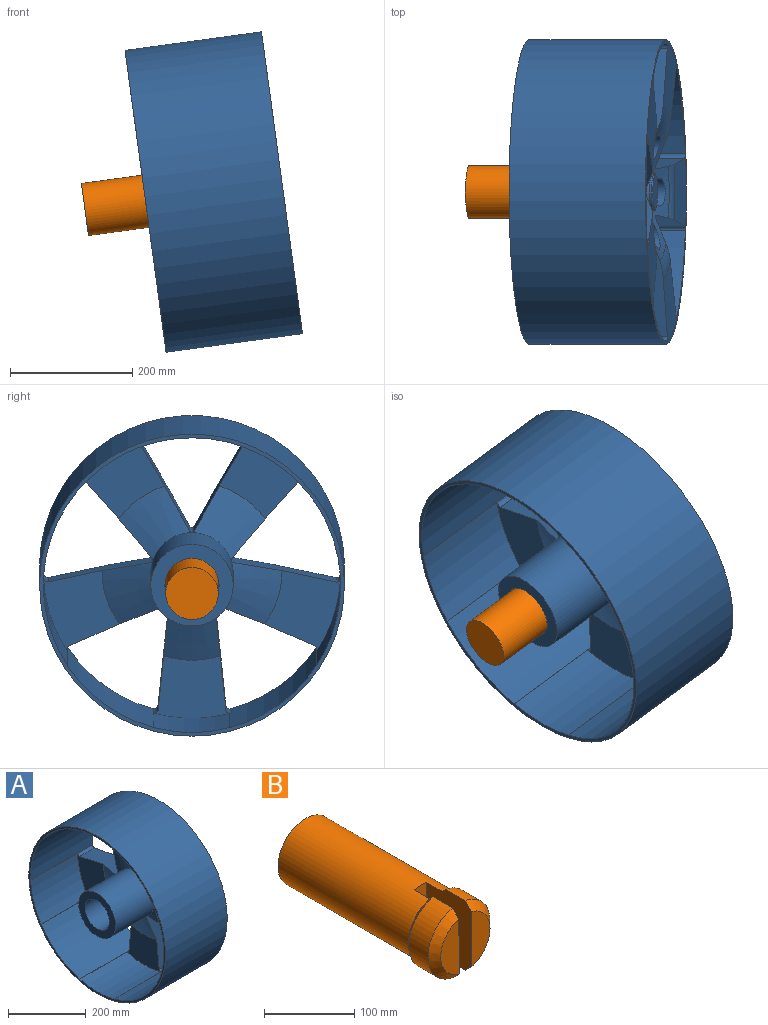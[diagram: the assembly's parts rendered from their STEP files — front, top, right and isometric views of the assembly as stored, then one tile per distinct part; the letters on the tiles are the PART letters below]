
ASSEMBLY  parts=2 mates=1
PART A: 145 faces, bbox 226x499.5x499.5 mm
  f0: cone r=67.37mm half-angle=69.4deg, axis (1,0,0), area 7405mm2, adj f36,f40,f42,f45,f134,f139
  f1: cone r=67.37mm half-angle=69.4deg, axis (1,0,0), area 7405mm2, adj f42,f46,f48,f51,f134,f135
  f2: cone r=67.37mm half-angle=69.4deg, axis (1,0,0), area 7405mm2, adj f24,f27,f48,f52,f134,f141
  f3: cone r=67.37mm half-angle=69.4deg, axis (1,0,0), area 7405mm2, adj f24,f28,f30,f33,f134,f143
  f4: plane 134.73x134.73mm, normal (-1,0,0), area 8092.4mm2, adj f129,f134
  f5: cone r=124.45mm half-angle=70.8deg, axis (1,0,0), area 14731.5mm2, adj f10,f11,f12,f13,f14,f20,f24,f27
  f6: cone r=243.25mm half-angle=87.6deg, axis (1,0,0), area 10747.7mm2, adj f10,f22,f44,f46,f49,f51
  f7: cone r=243.25mm half-angle=87.6deg, axis (1,0,0), area 10747.7mm2, adj f11,f22,f38,f40,f43,f45
  f8: cone r=243.25mm half-angle=87.6deg, axis (1,0,0), area 10747.7mm2, adj f12,f22,f32,f34,f37,f39
  f9: cone r=243.25mm half-angle=87.6deg, axis (1,0,0), area 10747.7mm2, adj f13,f22,f26,f28,f31,f33
  f10: torus R=143.39mm, axis (-1,0,0), area 2642.4mm2, adj f5,f6,f46,f51
  f11: torus R=143.39mm, axis (-1,0,0), area 2642.4mm2, adj f5,f7,f40,f45
  f12: torus R=143.39mm, axis (-1,0,0), area 2642.4mm2, adj f5,f8,f34,f39
  f13: torus R=143.39mm, axis (-1,0,0), area 2642.4mm2, adj f5,f9,f28,f33
  f14: torus R=143.39mm, axis (-1,0,0), area 2642.4mm2, adj f5,f21,f27,f52
  f15: plane 498.71x498.71mm, normal (-1,0,0), area 9451.9mm2, adj f23,f25,f26,f29,f31,f32,f35,f37
  f16: plane 56.3x56.3mm, normal (1,0,0), area 2489.8mm2, adj f17
  f17: torus R=28.15mm, axis (1,0,0), area 580.8mm2, adj f16,f18
  f18: cylinder r=30.15mm len=60.3mm, axis (1,0,0), area 609.9mm2, adj f17,f19
  f19: torus R=35.15mm, axis (1,0,0), area 1577.6mm2, adj f18,f20
  f20: plane 116.68x114.86mm, normal (1,0,0), area 6129.8mm2, adj f5,f19,f54,f56,f58,f60,f62
  f21: cone r=243.25mm half-angle=87.6deg, axis (1,0,0), area 10747.7mm2, adj f14,f22,f25,f27,f50,f52
  f22: plane 498.71x498.71mm, normal (1,0,0), area 9437.7mm2, adj f6,f7,f8,f9,f21,f23,f29,f35
  f23: cylinder r=249.35mm len=498.71mm, axis (1,0,0), area 352851.2mm2, adj f15,f22
  f24: cylinder r=4.19mm len=60.02mm, axis (1,0,0), area 475mm2, adj f2,f3,f5,f27,f28
  f25: cylinder r=5.94mm len=225.22mm, axis (1,0,0), area 527.7mm2, adj f15,f21,f27,f29,f140,f141
  f26: cylinder r=7.54mm len=225.22mm, axis (1,0,0), area 632.1mm2, adj f9,f15,f28,f29,f142,f143
  f27: plane 150.67x87.83mm, normal (0,0.86,0.5), area 9440.6mm2, adj f2,f5,f14,f21,f24,f25,f141
  f28: plane 149.15x86.95mm, normal (0,-0.86,0.5), area 9346.9mm2, adj f3,f5,f9,f13,f24,f26,f143
  f29: cylinder r=243.25mm len=225.22mm, axis (1,0,0), area 40182.8mm2, adj f15,f22,f25,f26
  f30: cylinder r=4.19mm len=60.02mm, axis (1,0,0), area 475mm2, adj f3,f5,f33,f34,f144
  f31: cylinder r=5.94mm len=225.22mm, axis (1,0,0), area 527.7mm2, adj f9,f15,f33,f35,f142,f143
  f32: cylinder r=7.54mm len=225.22mm, axis (1,0,0), area 632.1mm2, adj f8,f15,f34,f35,f136,f137
  f33: plane 129.88x116.43mm, normal (0,0.74,-0.67), area 9440.6mm2, adj f3,f5,f9,f13,f30,f31,f143
  f34: plane 168.52x83.99mm, normal (0,0.21,0.98), area 9346.9mm2, adj f5,f8,f12,f30,f32,f137,f144
  f35: cylinder r=243.25mm len=225.22mm, axis (1,0,0), area 40182.8mm2, adj f15,f22,f31,f32
  f36: cylinder r=4.19mm len=60.02mm, axis (1,0,0), area 475mm2, adj f0,f5,f39,f40,f144
  f37: cylinder r=5.94mm len=225.22mm, axis (1,0,0), area 527.7mm2, adj f8,f15,f39,f41,f136,f137
  f38: cylinder r=7.54mm len=225.22mm, axis (1,0,0), area 632.1mm2, adj f7,f15,f40,f41,f138,f139
  f39: plane 159.3x84.01mm, normal (0,-0.4,-0.91), area 9440.6mm2, adj f5,f8,f12,f36,f37,f137,f144
  f40: plane 171.46x83.99mm, normal (0,0.99,0.1), area 9346.9mm2, adj f0,f5,f7,f11,f36,f38,f139
  f41: cylinder r=243.25mm len=225.22mm, axis (1,0,0), area 40182.8mm2, adj f15,f22,f37,f38
  f42: cylinder r=4.19mm len=60.02mm, axis (1,0,0), area 475mm2, adj f0,f1,f5,f45,f46
  f43: cylinder r=5.94mm len=225.22mm, axis (1,0,0), area 527.7mm2, adj f7,f15,f45,f47,f138,f139
  f44: cylinder r=7.54mm len=225.22mm, axis (1,0,0), area 632.1mm2, adj f6,f15,f46,f47,f133,f135
  f45: plane 173.21x84.02mm, normal (0,-0.99,0.1), area 9440.6mm2, adj f0,f5,f7,f11,f42,f43,f139
  f46: plane 157.7x83.99mm, normal (0,0.4,-0.91), area 9346.9mm2, adj f1,f5,f6,f10,f42,f44,f135
  f47: cylinder r=243.25mm len=225.22mm, axis (1,0,0), area 40182.8mm2, adj f15,f22,f43,f44
  f48: cylinder r=4.19mm len=60.02mm, axis (1,0,0), area 475mm2, adj f1,f2,f5,f51,f52
  f49: cylinder r=5.94mm len=225.22mm, axis (1,0,0), area 527.7mm2, adj f6,f15,f51,f53,f133,f135
  f50: cylinder r=7.54mm len=225.22mm, axis (1,0,0), area 632.1mm2, adj f15,f21,f52,f53,f140,f141
  f51: plane 170.23x84.02mm, normal (0,-0.21,0.98), area 9440.6mm2, adj f1,f5,f6,f10,f48,f49,f135
  f52: plane 128.58x115.26mm, normal (0,-0.74,-0.67), area 9346.9mm2, adj f2,f5,f14,f21,f48,f50,f141
  f53: cylinder r=243.25mm len=225.22mm, axis (1,0,0), area 40182.8mm2, adj f15,f22,f49,f50
  f54: cylinder r=23mm len=46mm, axis (1,0,0), area 4559.1mm2, adj f5,f20,f55
  f55: plane 46x46mm, normal (1,0,0), area 806.5mm2, adj f54,f64,f65,f66,f67,f68,f69
  f56: cylinder r=23mm len=46mm, axis (1,0,0), area 4559.5mm2, adj f5,f20,f57
  f57: plane 46x46mm, normal (1,0,0), area 806.5mm2, adj f56,f71,f72,f73,f74,f75,f76
  f58: cylinder r=23mm len=46mm, axis (1,0,0), area 4559.8mm2, adj f5,f20,f59
  f59: plane 46x46mm, normal (1,0,0), area 806.5mm2, adj f58,f78,f79,f80,f81,f82,f83
  f60: cylinder r=23mm len=46mm, axis (1,0,0), area 4559.8mm2, adj f5,f20,f61
  f61: plane 46x46mm, normal (1,0,0), area 806.5mm2, adj f60,f85,f86,f87,f88,f89,f90
  f62: cylinder r=23mm len=46mm, axis (1,0,0), area 4561.5mm2, adj f5,f20,f63
  f63: plane 46x46mm, normal (1,0,0), area 806.5mm2, adj f62,f92,f93,f94,f95,f96,f97
  f64: plane 19x18.14mm, normal (0,-0.01,1), area 344.8mm2, adj f55,f65,f69,f124
  f65: plane 19x15.83mm, normal (0,-0.87,0.49), area 344.8mm2, adj f55,f64,f66,f123
  f66: plane 19x15.6mm, normal (0,-0.86,-0.51), area 344.8mm2, adj f55,f65,f67,f125
  f67: plane 19x18.14mm, normal (0,0.01,-1), area 344.8mm2, adj f55,f66,f68,f127
  f68: plane 19x15.83mm, normal (0,0.87,-0.49), area 344.8mm2, adj f55,f67,f69,f128
  f69: plane 19x15.6mm, normal (0,0.86,0.51), area 344.8mm2, adj f55,f64,f68,f126
  f70: plane 31.67x27.63mm, normal (1,0,0), area 651.6mm2, adj f123,f124,f125,f126,f127,f128
  f71: plane 19x17.33mm, normal (0,-0.95,0.3), area 344.8mm2, adj f57,f72,f76,f118
  f72: plane 19x13.33mm, normal (0,-0.73,-0.68), area 344.8mm2, adj f57,f71,f73,f117
  f73: plane 19x17.7mm, normal (0,0.22,-0.98), area 344.8mm2, adj f57,f72,f74,f119
  f74: plane 19x17.33mm, normal (0,0.95,-0.3), area 344.8mm2, adj f57,f73,f75,f121
  f75: plane 19x13.33mm, normal (0,0.73,0.68), area 344.8mm2, adj f57,f74,f76,f122
  f76: plane 19x17.7mm, normal (0,-0.22,0.98), area 344.8mm2, adj f57,f71,f75,f120
  f77: plane 30.89x30.24mm, normal (1,0,0), area 651.6mm2, adj f117,f118,f119,f120,f121,f122
  f78: plane 19x14.82mm, normal (0,-0.58,-0.82), area 344.8mm2, adj f59,f79,f83,f112
  f79: plane 19x16.48mm, normal (0,0.42,-0.91), area 344.8mm2, adj f59,f78,f80,f111
  f80: plane 19x18.07mm, normal (0,1,-0.09), area 344.8mm2, adj f59,f79,f81,f113
  f81: plane 19x14.82mm, normal (0,0.58,0.82), area 344.8mm2, adj f59,f80,f82,f115
  f82: plane 19x16.48mm, normal (0,-0.42,0.91), area 344.8mm2, adj f59,f81,f83,f116
  f83: plane 19x18.07mm, normal (0,-1,0.09), area 344.8mm2, adj f59,f78,f82,f114
  f84: plane 31.54x28.77mm, normal (1,0,0), area 651.6mm2, adj f111,f112,f113,f114,f115,f116
  f85: plane 19x14.54mm, normal (0,0.6,-0.8), area 344.8mm2, adj f61,f86,f90,f106
  f86: plane 19x18.02mm, normal (0,0.99,0.12), area 344.8mm2, adj f61,f85,f87,f105
  f87: plane 19x16.67mm, normal (0,0.4,0.92), area 344.8mm2, adj f61,f86,f88,f107
  f88: plane 19x14.54mm, normal (0,-0.6,0.8), area 344.8mm2, adj f61,f87,f89,f109
  f89: plane 19x18.02mm, normal (0,-0.99,-0.12), area 344.8mm2, adj f61,f88,f90,f110
  f90: plane 19x16.67mm, normal (0,-0.4,-0.92), area 344.8mm2, adj f61,f85,f89,f108
  f91: plane 31.45x29.1mm, normal (1,0,0), area 651.6mm2, adj f105,f106,f107,f108,f109,f110
  f92: plane 19x17.18mm, normal (0,0.95,0.32), area 344.8mm2, adj f63,f93,f97,f100
  f93: plane 19x17.8mm, normal (0,0.2,0.98), area 344.8mm2, adj f63,f92,f94,f99
  f94: plane 19x13.64mm, normal (0,-0.75,0.66), area 344.8mm2, adj f63,f93,f95,f101
  f95: plane 19x17.18mm, normal (0,-0.95,-0.32), area 344.8mm2, adj f63,f94,f96,f103
  f96: plane 19x17.8mm, normal (0,-0.2,-0.98), area 344.8mm2, adj f63,f95,f97,f104
  f97: plane 19x13.64mm, normal (0,0.75,-0.66), area 344.8mm2, adj f63,f92,f96,f102
  f98: plane 31.06x30mm, normal (1,0,0), area 651.6mm2, adj f99,f100,f101,f102,f103,f104
  f99: cylinder r=2mm len=18.19mm, axis (0,0.98,-0.2), area 53.4mm2, adj f93,f98,f100,f101
  f100: cylinder r=2mm len=17.83mm, axis (0,0.32,-0.95), area 53.4mm2, adj f92,f98,f99,f102
  f101: cylinder r=2mm len=14.96mm, axis (0,0.66,0.75), area 53.4mm2, adj f94,f98,f99,f103
  f102: cylinder r=2mm len=14.96mm, axis (0,-0.66,-0.75), area 53.4mm2, adj f97,f98,f100,f104
  f103: cylinder r=2mm len=17.83mm, axis (0,-0.32,0.95), area 53.4mm2, adj f95,f98,f101,f104
  f104: cylinder r=2mm len=18.19mm, axis (0,-0.98,0.2), area 53.4mm2, adj f96,f98,f102,f103
  f105: cylinder r=2mm len=18.26mm, axis (0,0.12,-0.99), area 53.4mm2, adj f86,f91,f106,f107
  f106: cylinder r=2mm len=15.74mm, axis (0,-0.8,-0.6), area 53.4mm2, adj f85,f91,f105,f108
  f107: cylinder r=2mm len=17.46mm, axis (0,0.92,-0.4), area 53.4mm2, adj f87,f91,f105,f109
  f108: cylinder r=2mm len=17.46mm, axis (0,-0.92,0.4), area 53.4mm2, adj f90,f91,f106,f110
  f109: cylinder r=2mm len=15.74mm, axis (0,0.8,0.6), area 53.4mm2, adj f88,f91,f107,f110
  f110: cylinder r=2mm len=18.26mm, axis (0,-0.12,0.99), area 53.4mm2, adj f89,f91,f108,f109
  f111: cylinder r=2mm len=17.32mm, axis (0,-0.91,-0.42), area 53.4mm2, adj f79,f84,f112,f113
  f112: cylinder r=2mm len=15.97mm, axis (0,-0.82,0.58), area 53.4mm2, adj f78,f84,f111,f114
  f113: cylinder r=2mm len=18.25mm, axis (0,-0.09,-1), area 53.4mm2, adj f80,f84,f111,f115
  f114: cylinder r=2mm len=18.25mm, axis (0,0.09,1), area 53.4mm2, adj f83,f84,f112,f116
  f115: cylinder r=2mm len=15.97mm, axis (0,0.82,-0.58), area 53.4mm2, adj f81,f84,f113,f116
  f116: cylinder r=2mm len=17.32mm, axis (0,0.91,0.42), area 53.4mm2, adj f82,f84,f114,f115
  f117: cylinder r=2mm len=14.69mm, axis (0,-0.68,0.73), area 53.4mm2, adj f72,f77,f118,f119
  f118: cylinder r=2mm len=17.92mm, axis (0,0.3,0.95), area 53.4mm2, adj f71,f77,f117,f120
  f119: cylinder r=2mm len=18.14mm, axis (0,-0.98,-0.22), area 53.4mm2, adj f73,f77,f117,f121
  f120: cylinder r=2mm len=18.14mm, axis (0,0.98,0.22), area 53.4mm2, adj f76,f77,f118,f122
  f121: cylinder r=2mm len=17.92mm, axis (0,-0.3,-0.95), area 53.4mm2, adj f74,f77,f119,f122
  f122: cylinder r=2mm len=14.69mm, axis (0,0.68,-0.73), area 53.4mm2, adj f75,f77,f120,f121
  f123: cylinder r=2mm len=16.81mm, axis (0,0.49,0.87), area 53.4mm2, adj f65,f70,f124,f125
  f124: cylinder r=2mm len=18.17mm, axis (0,1,0.01), area 53.4mm2, adj f64,f70,f123,f126
  f125: cylinder r=2mm len=16.62mm, axis (0,-0.51,0.86), area 53.4mm2, adj f66,f70,f123,f127
  f126: cylinder r=2mm len=16.62mm, axis (0,0.51,-0.86), area 53.4mm2, adj f69,f70,f124,f128
  f127: cylinder r=2mm len=18.17mm, axis (0,-1,-0.01), area 53.4mm2, adj f67,f70,f125,f128
  f128: cylinder r=2mm len=16.81mm, axis (0,-0.49,-0.87), area 53.4mm2, adj f68,f70,f126,f127
  f129: cylinder r=44.3mm len=100mm, axis (-1,0,0), area 27832.2mm2, adj f4,f130
  f130: plane 110.47x110.47mm, normal (1,0,0), area 3420.3mm2, adj f129,f131
  f131: cylinder r=55.23mm len=110.47mm, axis (-1,0,0), area 17352.6mm2, adj f130,f132
  f132: plane 110.47x110.47mm, normal (-1,0,0), area 9584.7mm2, adj f131
  f133: cylinder r=243.23mm len=171mm, axis (-1,0,0), area 21705.5mm2, adj f15,f44,f49,f135
  f134: cylinder r=67.37mm len=141mm, axis (-1,0,0), area 59680.7mm2, adj f0,f1,f2,f3,f4,f144
  f135: plane 133.6x124.09mm, normal (-1,0,0), area 9971.5mm2, adj f1,f44,f46,f49,f51,f133
  f136: cylinder r=243.23mm len=171mm, axis (-1,0,0), area 21705.5mm2, adj f15,f32,f37,f137
  f137: plane 132.55x124.16mm, normal (-1,0,0), area 9971.5mm2, adj f32,f34,f37,f39,f136,f144
  f138: cylinder r=243.23mm len=171mm, axis (-1,0,0), area 21705.5mm2, adj f15,f38,f43,f139
  f139: plane 125.5x103.32mm, normal (-1,0,0), area 9971.5mm2, adj f0,f38,f40,f43,f45,f138
  f140: cylinder r=243.23mm len=171mm, axis (-1,0,0), area 21705.5mm2, adj f15,f25,f50,f141
  f141: plane 144.49x140.79mm, normal (-1,0,0), area 9971.5mm2, adj f2,f25,f27,f50,f52,f140
  f142: cylinder r=243.23mm len=171mm, axis (-1,0,0), area 21705.5mm2, adj f15,f26,f31,f143
  f143: plane 143.7x141.24mm, normal (-1,0,0), area 9971.5mm2, adj f3,f26,f28,f31,f33,f142
  f144: cone r=67.37mm half-angle=69.4deg, axis (1,0,0), area 7405mm2, adj f30,f34,f36,f39,f134,f137
PART B: 13 faces, bbox 97.3x250.3x95.5 mm
  f0: cylinder r=48.5mm len=94.99mm, axis (0,1,0), area 3979.2mm2, adj f7,f9,f12
  f1: plane 74.46x29.15mm, normal (0,-1,0), area 1582.3mm2, adj f8,f11
  f2: cylinder r=48.5mm len=94.99mm, axis (0,1,0), area 3979.2mm2, adj f8,f10,f11
  f3: plane 74.46x29.15mm, normal (0,-1,0), area 1582.3mm2, adj f7,f12
  f4: cylinder r=43mm len=204.5mm, axis (0,1,0), area 54282.7mm2, adj f5,f6,f7,f8,f9,f10
  f5: plane 86x86mm, normal (0,1,0), area 5808.8mm2, adj f4
  f6: plane 86x20.6mm, normal (0,-1,0), area 1670.1mm2, adj f4,f7,f8
  f7: plane 95.27x70.27mm, normal (1,0,0.01), area 6240.7mm2, adj f0,f3,f4,f6,f9,f12
  f8: plane 95.27x70.27mm, normal (-1,0,-0.01), area 6240.7mm2, adj f1,f2,f4,f6,f10,f11
  f9: cone r=48.5mm half-angle=45deg, axis (0,-1,0), area 964mm2, adj f0,f4,f7
  f10: cone r=48.5mm half-angle=45deg, axis (0,-1,0), area 964mm2, adj f2,f4,f8
  f11: cone r=38.5mm half-angle=45deg, axis (0,1,0), area 1650.6mm2, adj f1,f2,f8
  f12: cone r=38.5mm half-angle=45deg, axis (0,1,0), area 1650.6mm2, adj f0,f3,f7
PLACE A rot(axis=(0,-1,0),7.7deg) t=(-128.21,22.95,-149.5)mm
PLACE B rot(axis=(0.53,-0.6,0.6),124.6deg) t=(-414.81,22.95,-247.63)mm
MATE revolute B.f0 <-> A.f131  axis (0.99,0,0.13) through (-167.09,22.95,-213.93)mm
